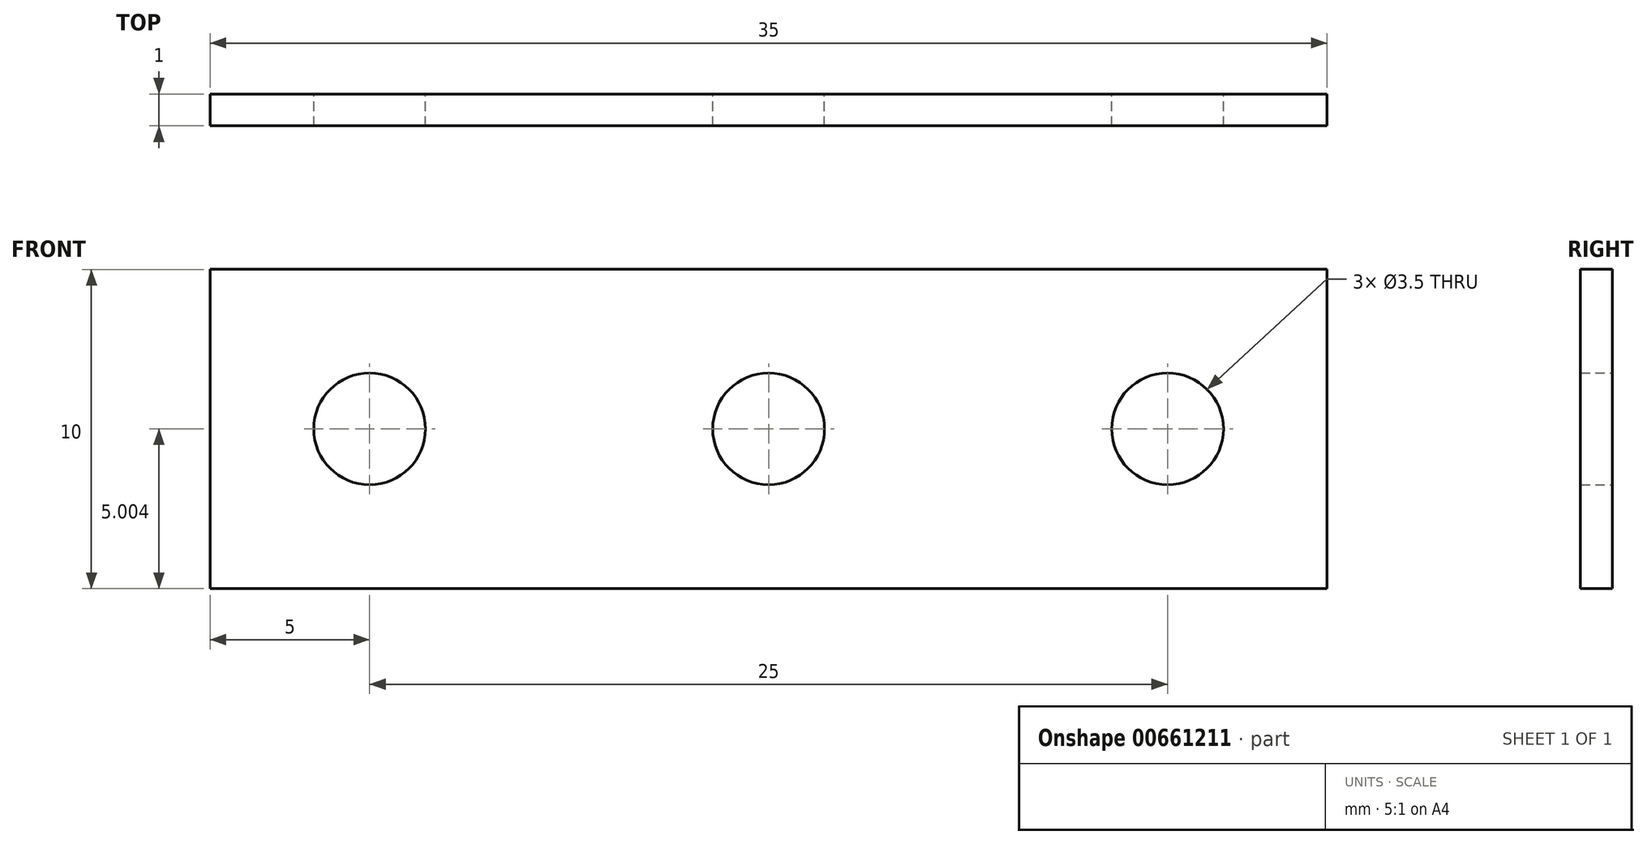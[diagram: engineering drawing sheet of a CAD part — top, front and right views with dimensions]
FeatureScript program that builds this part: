
annotation { "Feature Type Name" : "Feature", "Feature Type Description" : "" }
export const myFeature = defineFeature(function(context is Context, id is Id, definition is map)
    precondition{}
    {
        {
            var Q0;
            Q0=qCreatedBy(makeId("Front.planeOp"),FACE);
            var sketch = newSketch(context, id + "F0", { "sketchPlane" : qUnion([Q0])});
            skLineSegment(sketch, "E0", {"start": v(-17.5, 8.65) * mm, "end": v(17.5, 8.65) * mm});
            skLineSegment(sketch, "E1", {"start": v(17.5, 8.65) * mm, "end": v(17.5, -1.35) * mm});
            skLineSegment(sketch, "E2", {"start": v(17.5, -1.35) * mm, "end": v(-17.5, -1.35) * mm});
            skLineSegment(sketch, "E3", {"start": v(-17.5, -1.35) * mm, "end": v(-17.5, 8.65) * mm});
            skLineSegment(sketch, "E4", {"start": v(-17.5, -1.35) * mm, "end": v(-12.5, -1.35) * mm});
            skLineSegment(sketch, "E5", {"start": v(-12.5, -1.35) * mm, "end": v(-12.5, 3.65) * mm});
            skCircle(sketch, "E6", {"center": v(-12.5, 3.65) * mm, "radius": 1.75 * mm});
            skLineSegment(sketch, "E7", {"start": v(17.5, -1.35) * mm, "end": v(12.5, -1.35) * mm});
            skLineSegment(sketch, "E8", {"start": v(12.5, -1.35) * mm, "end": v(12.5, 3.65) * mm});
            skCircle(sketch, "E9", {"center": v(12.5, 3.65) * mm, "radius": 1.75 * mm});
            skLineSegment(sketch, "E10", {"start": v(12.5, 3.65) * mm, "end": v(0, 3.65) * mm});
            skCircle(sketch, "E11", {"center": v(0, 3.65) * mm, "radius": 1.75 * mm});
            skSolve(sketch);
        }
        {
            var Q0;
            Q0=qSketchRegion(id+"F0",true);
            var Q1;
            Q1=makeQuery(id+"F0.imprint","IMPRINT",FACE,{"disambiguationData":[TD([[makeQuery(id+"F0.imprint","IMPRINT",EDGE,{"derivedFrom":sQuery(id+"F0.wireOp",EDGE,"E0")}),-1.0]])]});
            extrude(context, id + "F1", {"entities" : qUnion([Q0, Q1]), "depth" : 1 * mm, "offsetDistance" : 25.4 * mm});
        }
        {
            var Q0;
            Q0=makeQuery(id+"F1.opExtrude","CAP_FACE",FACE,{"disambiguationData":[OSD([sQuery(id+"F0.wireOp",EDGE,"E0"),sQuery(id+"F0.wireOp",EDGE,"E1"),sQuery(id+"F0.wireOp",EDGE,"E2"),sQuery(id+"F0.wireOp",EDGE,"E3"),sQuery(id+"F0.wireOp",EDGE,"E4"),sQuery(id+"F0.wireOp",EDGE,"E6"),sQuery(id+"F0.wireOp",EDGE,"E7"),sQuery(id+"F0.wireOp",EDGE,"E9"),sQuery(id+"F0.wireOp",EDGE,"E11")])],"isStart":false});
            extrude(context, id + "F2", {"entities" : qUnion([Q0]), "operationType" : NewBodyOperationType.ADD, "oppositeDirection" : true, "depth" : 1 * mm, "offsetDistance" : 25.4 * mm});
        }
    });
